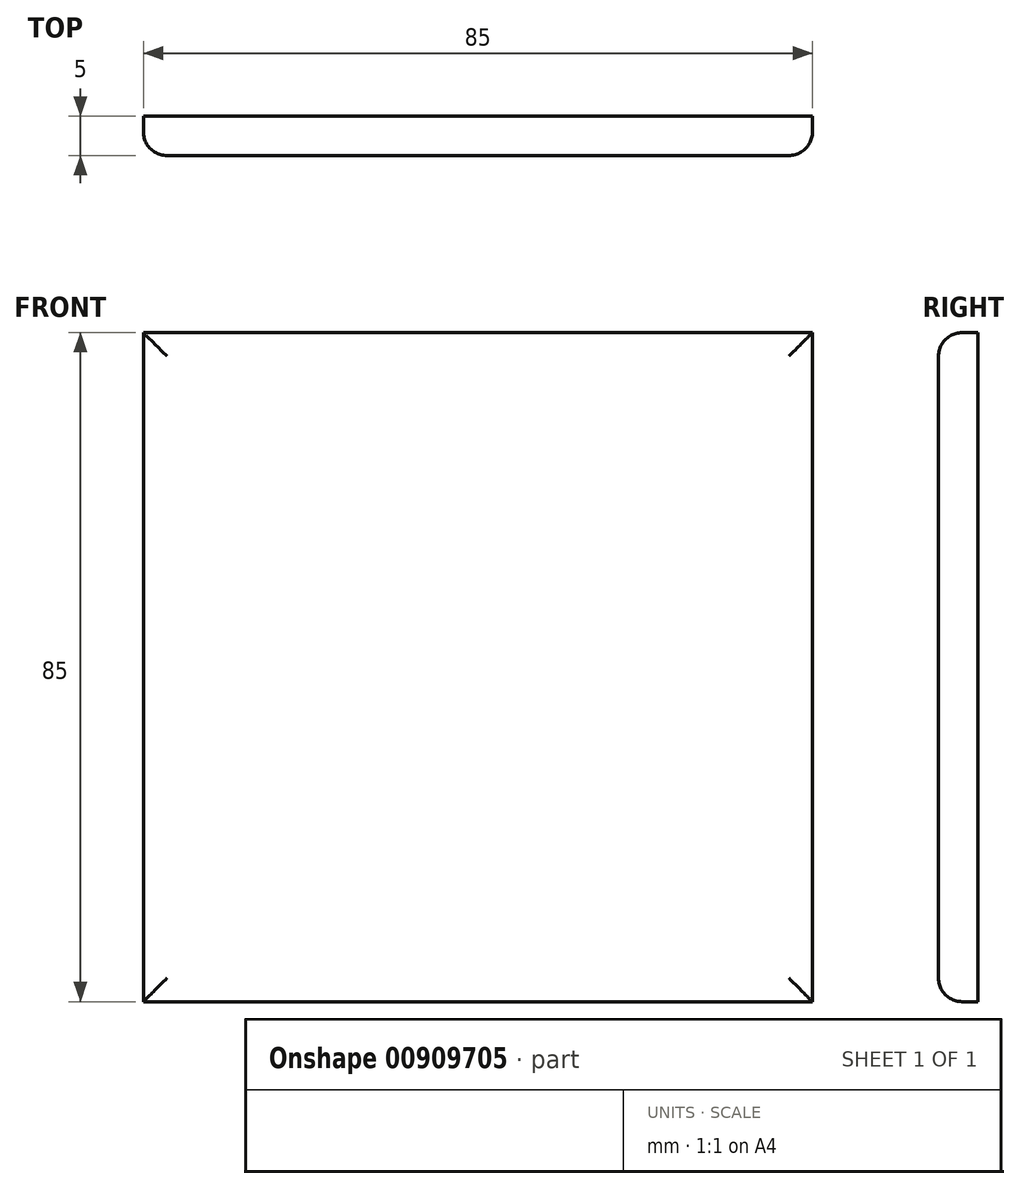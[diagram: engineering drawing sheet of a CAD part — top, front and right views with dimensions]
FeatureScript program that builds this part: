
annotation { "Feature Type Name" : "Feature", "Feature Type Description" : "" }
export const myFeature = defineFeature(function(context is Context, id is Id, definition is map)
    precondition{}
    {
        {
            var Q0;
            Q0=qCreatedBy(makeId("Front.planeOp"),FACE);
            var sketch = newSketch(context, id + "F0", { "sketchPlane" : qUnion([Q0])});
            skLineSegment(sketch, "E0.bottom", {"start": v(0, 0) * mm, "end": v(85, 0) * mm});
            skLineSegment(sketch, "E0.top", {"start": v(0, -85) * mm, "end": v(85, -85) * mm});
            skLineSegment(sketch, "E0.left", {"start": v(0, 0) * mm, "end": v(0, -85) * mm});
            skLineSegment(sketch, "E0.right", {"start": v(85, 0) * mm, "end": v(85, -85) * mm});
            skSolve(sketch);
        }
        {
            var Q0;
            Q0=makeQuery(id+"F0.imprint","IMPRINT",FACE,{"disambiguationData":[TD([[makeQuery(id+"F0.imprint","IMPRINT",EDGE,{"derivedFrom":sQuery(id+"F0.wireOp",EDGE,"E0.bottom")}),-1.0]])]});
            extrude(context, id + "F1", {"entities" : qUnion([Q0]), "depth" : 5 * mm, "offsetDistance" : 25 * mm});
        }
        {
            var Q0;
            Q0=makeQuery(id+"F1.opExtrude","CAP_EDGE",EDGE,{"disambiguationData":[OSD([sQuery(id+"F0.wireOp",EDGE,"E0.left")])],"isStart":false});
            var Q1;
            Q1=makeQuery(id+"F1.opExtrude","CAP_EDGE",EDGE,{"disambiguationData":[OSD([sQuery(id+"F0.wireOp",EDGE,"E0.bottom")])],"isStart":false});
            var Q2;
            Q2=makeQuery(id+"F1.opExtrude","CAP_EDGE",EDGE,{"disambiguationData":[OSD([sQuery(id+"F0.wireOp",EDGE,"E0.right")])],"isStart":false});
            var Q3;
            Q3=makeQuery(id+"F1.opExtrude","CAP_EDGE",EDGE,{"disambiguationData":[OSD([sQuery(id+"F0.wireOp",EDGE,"E0.top")])],"isStart":false});
            fillet(context, id + "F2", {"entities" : qUnion([Q0, Q1, Q2, Q3]), "radius" : 3 * mm, "tangentPropagation" : true, "allowEdgeOverflow" : false});
        }
    });
